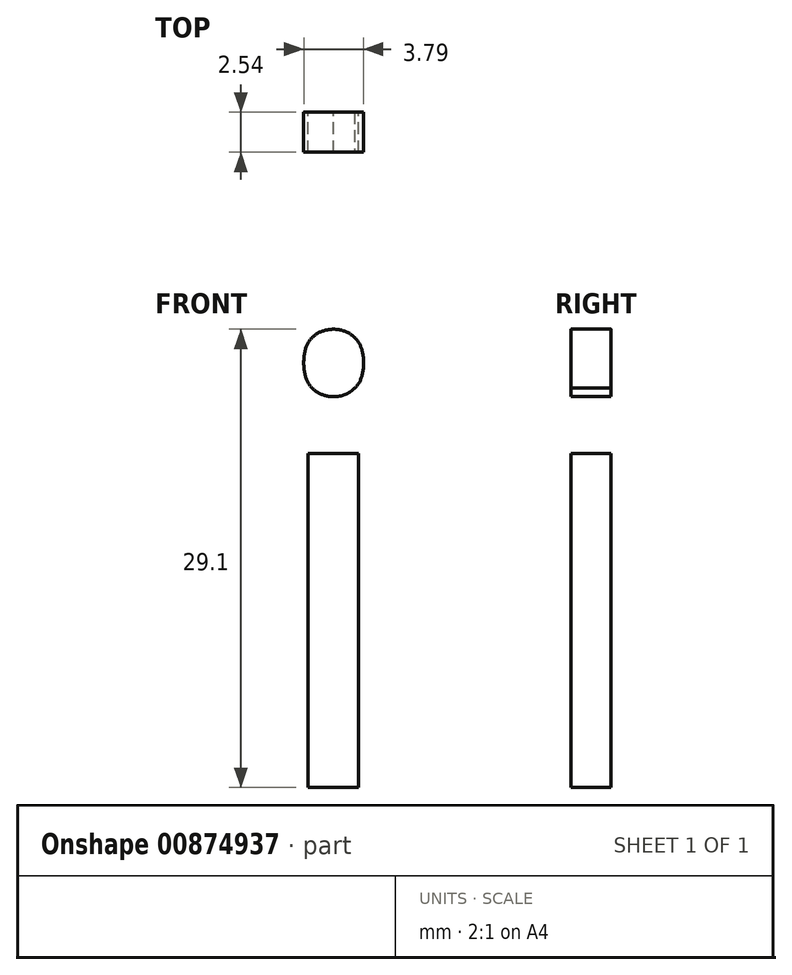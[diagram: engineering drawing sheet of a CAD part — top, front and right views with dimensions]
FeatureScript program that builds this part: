
annotation { "Feature Type Name" : "Feature", "Feature Type Description" : "" }
export const myFeature = defineFeature(function(context is Context, id is Id, definition is map)
    precondition{}
    {
        {
            var Q0;
            Q0=qCreatedBy(makeId("Front.planeOp"),FACE);
            var sketch = newSketch(context, id + "F0", { "sketchPlane" : qUnion([Q0])});
            skText(sketch, "E0", { "text": "i\n", "fontName": "OpenSans-Regular.ttf"});
            const initialGuessF0  = {"E0": [-0.0095, 0, 1, 0, 0.02855]};
            skSetInitialGuess(sketch, initialGuessF0);
            skSolve(sketch);
        }
        {
            var Q0;
            Q0 = qSketchRegion(id + "F0", true);
            extrude(context, id + "F1", {"entities" : qUnion([Q0]), "depth" : 2.54 * mm, "offsetDistance" : 25.4 * mm});
        }
    });
